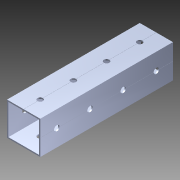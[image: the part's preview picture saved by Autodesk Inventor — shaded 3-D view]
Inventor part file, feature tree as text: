
AUTODESK INVENTOR PART (.ipt)
format: ipt  version: 2014 (Build 180170000, 170)  size: 1,130,496 bytes
history: native  units: in
note: dims shown in document units (in); Inventor stores cm internally (conversion verified against a paired STEP export)
features: pattern_circular x1, other x1, plane x1, extrude x1, imported_body x1, sketch x1
ambient origin geometry x8: Origin, YZ Plane, XZ Plane, XY Plane, X Axis, Y Axis, Z Axis, Center Point
bodies: Body1 (feature_tree)
feature tree (6):
  pattern_circular  "CirPattern2"
  other  "217-3426-STEP1"
  plane  "Work Plane1"
  extrude  "Extrusion1"  Depth=3937.0079in TaperAngle=0.0deg
  imported_body  "Base1"
  sketch  "Sketch1"  dims[d0=-4.0in d1=3937.0079in d2=0.0in]
